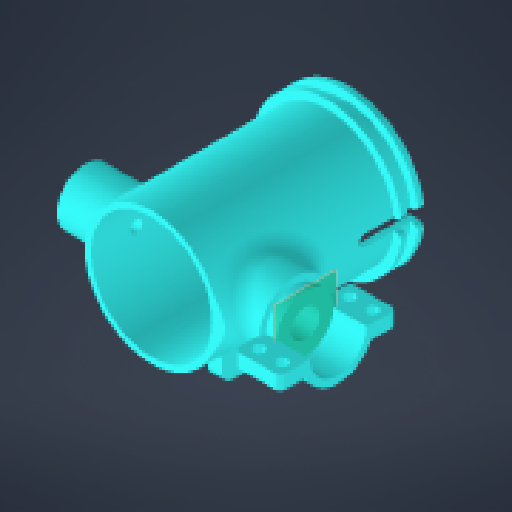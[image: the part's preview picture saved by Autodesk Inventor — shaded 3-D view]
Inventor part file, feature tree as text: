
AUTODESK INVENTOR PART (.ipt)
format: ipt  version: 2024 (Build 280153000, 153)  size: 524,288 bytes
history: native  units: mm
features: sketch x15, extrude x13, other x9, fillet x7, revolve x2, mirror x1
ambient origin geometry x8: Origin, YZ Plane, XZ Plane, XY Plane, X Axis, Y Axis, Z Axis, Center Point
bodies: Body1 (feature_tree)
feature tree (47):
  other  "Твердое тело1"
  extrude  "Выдавливание1"  Depth=70.0mm
  other  "РабПлоскость2"
  revolve  "Вращение1"
  fillet  "Сопряжение1"  [1 undecoded]
  extrude  "Выдавливание2"  Depth=47.0mm
  extrude  "Выдавливание3"  [1 undecoded]
  extrude  "Выдавливание4"  TaperAngle=90.0deg  [1 undecoded]
  fillet  "Сопряжение2"  Radius=10.0mm
  extrude  "Выдавливание5"  Depth=20.0mm
  revolve  "Вращение2"
  fillet  "Сопряжение3"  Radius=36.0mm
  extrude  "Выдавливание6"  TaperAngle=0.0deg  [1 undecoded]
  fillet  "Сопряжение4"  Radius=12.0mm
  fillet  "Сопряжение5"  Radius=5.0mm
  extrude  "Выдавливание8"  Depth=7.5mm
  extrude  "Выдавливание11"  Depth=40.0mm
  extrude  "Выдавливание12"  TaperAngle=0.0deg  [1 undecoded]
  fillet  "Сопряжение6"  Radius=3.0mm
  mirror  "Зеркальное отражение5"
  other  "РабПлоскость7"
  extrude  "Выдавливание14"  Depth=5.0mm
  extrude  "Выдавливание15"  Depth=8.0mm
  fillet  "Сопряжение7"  [1 undecoded]
  extrude  "Выдавливание16"  TaperAngle=0.0deg  [1 undecoded]
  other  "РабПлоскость8"
  extrude  "Выдавливание17"  Depth=4.0mm
  sketch  "Эскиз1"
  sketch  "Эскиз3"
  sketch  "Эскиз4"
  sketch  "Эскиз5"
  sketch  "Эскиз6"
  sketch  "Эскиз7"
  sketch  "Эскиз8"
  sketch  "Эскиз9"
  sketch  "Эскиз11"
  sketch  "Эскиз14"
  sketch  "Эскиз15"
  other  "РабПлоскость6"
  sketch  "Эскиз17"
  sketch  "Эскиз18"
  sketch  "Эскиз19"
  sketch  "Эскиз21"
  parser-record x1  (decoder bookkeeping rows leaked as tree rows — omitted from the tree; the rows remain in map.json)
  other  "rigt_motor_asembly.iam"
  other  "bushing_assembly:2"
  other  "bushing:1"
note: 7 required parameter values undecoded (feature->parameter linkage not recoverable at this tier; creation-order binding heuristic only, values carry confidence <= 0.55)
note: 1 file-system path scrubbed to <path> (originals preserved in map.json)
